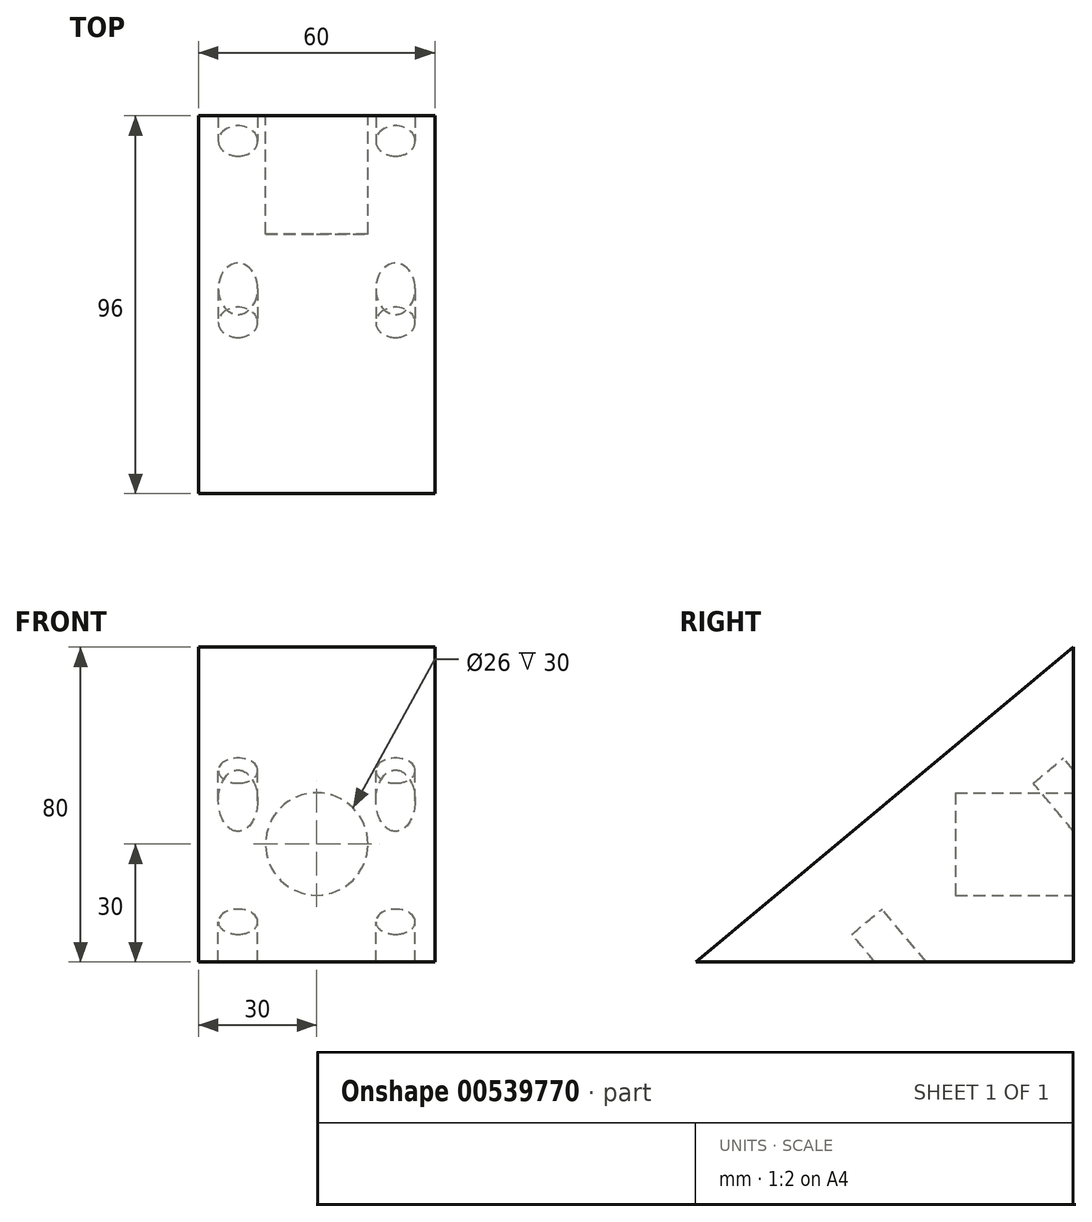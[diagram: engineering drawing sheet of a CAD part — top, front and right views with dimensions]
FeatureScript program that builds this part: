
annotation { "Feature Type Name" : "Feature", "Feature Type Description" : "" }
export const myFeature = defineFeature(function(context is Context, id is Id, definition is map)
    precondition{}
    {
        {
            var Q0;
            Q0=qCreatedBy(makeId("Right.planeOp"),FACE);
            var sketch = newSketch(context, id + "F0", { "sketchPlane" : qUnion([Q0])});
            skLineSegment(sketch, "E0.top", {"start": v(-48, -40) * mm, "end": v(48, -40) * mm});
            skLineSegment(sketch, "E0.right", {"start": v(48, 40) * mm, "end": v(48, -40) * mm});
            skLineSegment(sketch, "E1", {"start": v(-48, -40) * mm, "end": v(48, 40) * mm});
            skSolve(sketch);
        }
        {
            var Q0;
            Q0 = qSketchRegion(id + "F0", true);
            extrude(context, id + "F1", {"entities" : qUnion([Q0]), "endBound" : BoundingType.SYMMETRIC, "depth" : 60 * mm, "offsetDistance" : 25 * mm});
        }
        {
            var Q0;
            Q0=makeQuery(id+"F1.opExtrude","SWEPT_FACE",FACE,{"disambiguationData":[OSD([sQuery(id+"F0.wireOp",EDGE,"E0.right")])]});
            var sketch = newSketch(context, id + "F2", { "sketchPlane" : qUnion([Q0])});
            skCircle(sketch, "E2", {"center": v(0, -10) * mm, "radius": 13 * mm});
            skSolve(sketch);
        }
        {
            var Q0;
            Q0 = qSketchRegion(id + "F2", true);
            extrude(context, id + "F3", {"entities" : qUnion([Q0]), "operationType" : NewBodyOperationType.REMOVE, "oppositeDirection" : true, "depth" : 30 * mm, "offsetDistance" : 25 * mm});
        }
        {
            var Q0;
            Q0=makeQuery(id+"F1.opExtrude","SWEPT_FACE",FACE,{"disambiguationData":[OSD([sQuery(id+"F0.wireOp",EDGE,"E1")])]});
            cPlane(context, id + "F4", {"entities" : qUnion([Q0]), "cplaneType" : CPlaneType.OFFSET, "offset" : 20 * mm, "oppositeDirection" : true, "width" : 150 * mm, "height" : 150 * mm});
        }
        {
            var Q0;
            Q0=qCreatedBy(id+"F4.planeOp",FACE);
            var sketch = newSketch(context, id + "F5", { "sketchPlane" : qUnion([Q0])});
            skCircle(sketch, "E3", {"center": v(20, -22.48) * mm, "radius": 5 * mm});
            skCircle(sketch, "E4.0.1.0", {"center": v(20, 37.52) * mm, "radius": 5 * mm});
            skCircle(sketch, "E4.1.0.0", {"center": v(-20, -22.48) * mm, "radius": 5 * mm});
            skCircle(sketch, "E4.1.1.0", {"center": v(-20, 37.52) * mm, "radius": 5 * mm});
            skLineSegment(sketch, "E4.direction1", {"start": v(20, -22.48) * mm, "end": v(-20, -22.48) * mm, "construction": true});
            skLineSegment(sketch, "E4.direction2", {"start": v(20, -22.48) * mm, "end": v(20, 37.52) * mm, "construction": true});
            skSolve(sketch);
        }
        {
            var Q0;
            Q0 = qSketchRegion(id + "F5", true);
            extrude(context, id + "F6", {"entities" : qUnion([Q0]), "operationType" : NewBodyOperationType.REMOVE, "oppositeDirection" : true, "depth" : 25 * mm, "offsetDistance" : 25 * mm});
        }
    });
